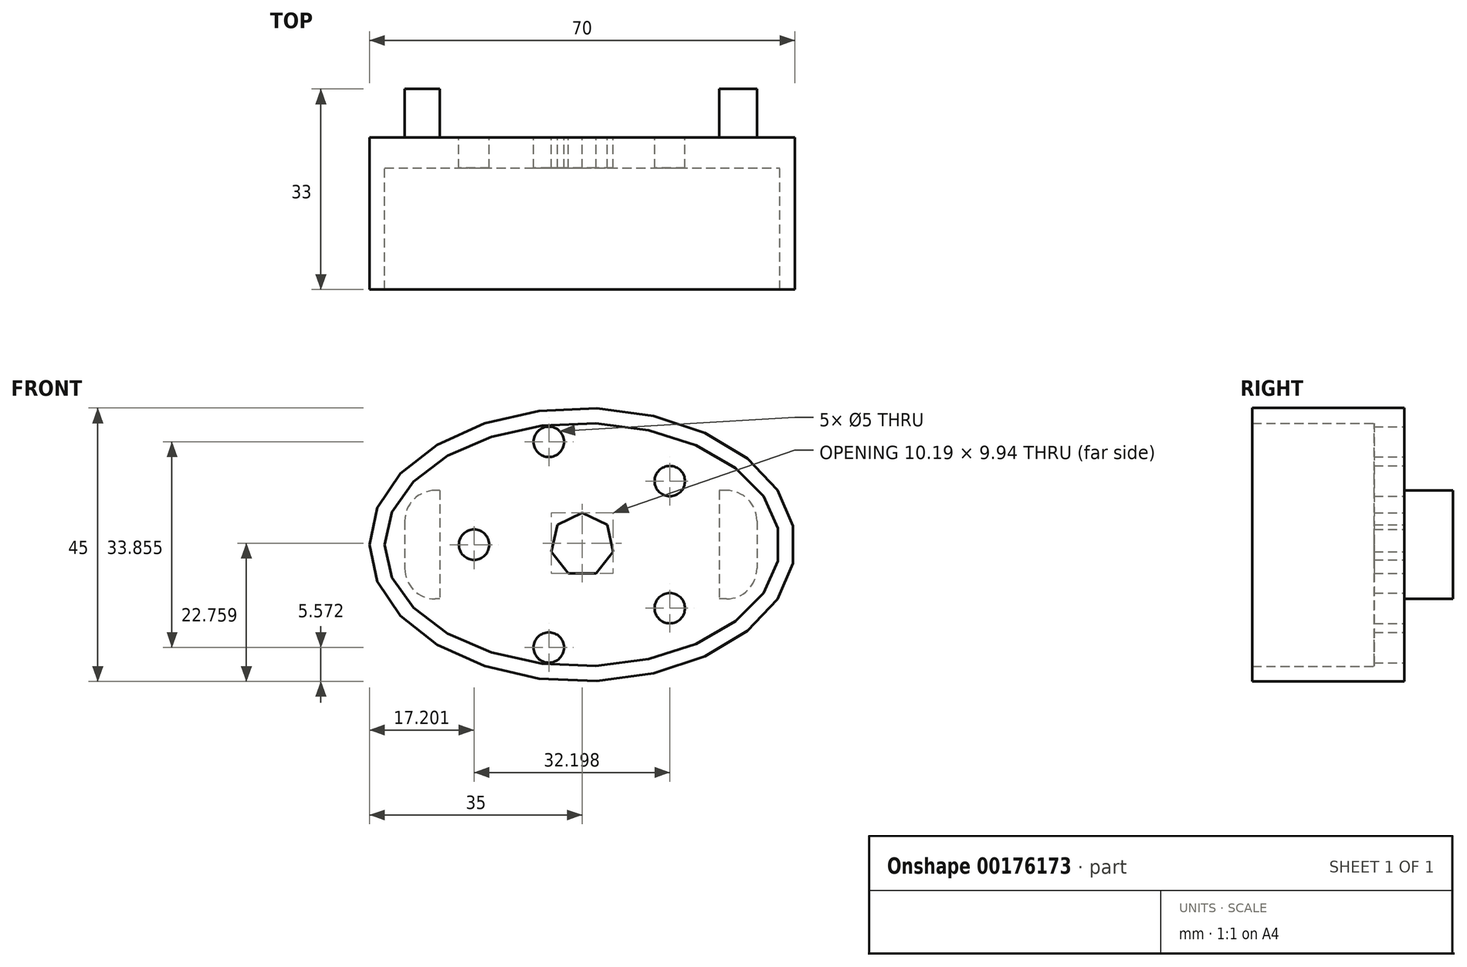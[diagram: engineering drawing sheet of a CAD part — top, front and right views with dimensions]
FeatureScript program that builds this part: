
annotation { "Feature Type Name" : "Feature", "Feature Type Description" : "" }
export const myFeature = defineFeature(function(context is Context, id is Id, definition is map)
    precondition{}
    {
        {
            var Q0;
            Q0=qCreatedBy(makeId("Front.planeOp"),FACE);
            var sketch = newSketch(context, id + "F0", { "sketchPlane" : qUnion([Q0])});
            skEllipse(sketch, "E0", {"center": v(0, 0) * mm, "majorRadius": 35 * mm, "minorRadius": 22.5 * mm, "majorAxis": v(-1, 0)});
            skSolve(sketch);
        }
        {
            var Q0;
            Q0=makeQuery(id+"F0.imprint","IMPRINT",FACE,{"disambiguationData":[TD([[makeQuery(id+"F0.imprint","IMPRINT",EDGE,{"derivedFrom":sQuery(id+"F0.wireOp",EDGE,"E0")}),1.0]])]});
            extrude(context, id + "F1", {"entities" : qUnion([Q0]), "depth" : 5 * mm});
        }
        {
            var Q0;
            Q0=makeQuery(id+"F1.opExtrude","CAP_FACE",FACE,{"disambiguationData":[OSD([sQuery(id+"F0.wireOp",EDGE,"E0")])],"isStart":false});
            var sketch = newSketch(context, id + "F2", { "sketchPlane" : qUnion([Q0])});
            skEllipse(sketch, "E1", {"center": v(0, 0) * mm, "majorRadius": 32.5 * mm, "minorRadius": 20 * mm, "majorAxis": v(-1, 0)});
            skSolve(sketch);
        }
        {
            var Q0;
            Q0=makeQuery(id+"F2.imprint","IMPRINT",FACE,{"disambiguationData":[TD([[makeQuery(id+"F2.imprint","IMPRINT",EDGE,{"derivedFrom":sQuery(id+"F2.wireOp",EDGE,"E1")}),-1.0]])]});
            extrude(context, id + "F3", {"entities" : qUnion([Q0]), "operationType" : NewBodyOperationType.ADD, "depth" : 20 * mm});
        }
        {
            var Q0;
            Q0=qCreatedBy(makeId("Front.planeOp"),FACE);
            var sketch = newSketch(context, id + "F4", { "sketchPlane" : qUnion([Q0])});
            skCircle(sketch, "E2", {"center": v(-17.8, 0) * mm, "radius": 2.5 * mm});
            skCircle(sketch, "E3.1.0", {"center": v(-5.5, -16.93) * mm, "radius": 2.5 * mm});
            skCircle(sketch, "E3.2.0", {"center": v(14.4, -10.46) * mm, "radius": 2.5 * mm});
            skCircle(sketch, "E3.3.0", {"center": v(14.4, 10.46) * mm, "radius": 2.5 * mm});
            skCircle(sketch, "E3.4.0", {"center": v(-5.5, 16.93) * mm, "radius": 2.5 * mm});
            skPoint(sketch, "E3.center", {"position": v(0, 0) * mm});
            skSolve(sketch);
        }
        {
            var Q0;
            Q0=makeQuery(id+"F1.opExtrude","CAP_FACE",FACE,{"disambiguationData":[OSD([sQuery(id+"F0.wireOp",EDGE,"E0")])],"isStart":true});
            var sketch = newSketch(context, id + "F5", { "sketchPlane" : qUnion([Q0])});
            skSolve(sketch);
        }
        {
            var Q0;
            Q0=makeQuery(id+"F4.imprint","IMPRINT",FACE,{"disambiguationData":[TD([[makeQuery(id+"F4.imprint","IMPRINT",EDGE,{"derivedFrom":sQuery(id+"F4.wireOp",EDGE,"E3.1.0")}),1.0]])]});
            var Q1;
            Q1=makeQuery(id+"F4.imprint","IMPRINT",FACE,{"disambiguationData":[TD([[makeQuery(id+"F4.imprint","IMPRINT",EDGE,{"derivedFrom":sQuery(id+"F4.wireOp",EDGE,"E3.2.0")}),1.0]])]});
            var Q2;
            Q2=makeQuery(id+"F4.imprint","IMPRINT",FACE,{"disambiguationData":[TD([[makeQuery(id+"F4.imprint","IMPRINT",EDGE,{"derivedFrom":sQuery(id+"F4.wireOp",EDGE,"E3.3.0")}),1.0]])]});
            var Q3;
            Q3=makeQuery(id+"F4.imprint","IMPRINT",FACE,{"disambiguationData":[TD([[makeQuery(id+"F4.imprint","IMPRINT",EDGE,{"derivedFrom":sQuery(id+"F4.wireOp",EDGE,"E3.4.0")}),1.0]])]});
            var Q4;
            Q4=makeQuery(id+"F4.imprint","IMPRINT",FACE,{"disambiguationData":[TD([[makeQuery(id+"F4.imprint","IMPRINT",EDGE,{"derivedFrom":sQuery(id+"F4.wireOp",EDGE,"E2")}),1.0]])]});
            extrude(context, id + "F6", {"entities" : qUnion([Q0, Q1, Q2, Q3, Q4]), "operationType" : NewBodyOperationType.REMOVE, "endBound" : BoundingType.THROUGH_ALL, "depth" : 25 * mm});
        }
        {
            var Q0;
            Q0=makeQuery(id+"F5.imprint","IMPRINT",FACE,{"disambiguationData":[TD([[makeQuery(id+"F5.imprint","IMPRINT",EDGE,{"derivedFrom":makeQuery(id+"F1.opExtrude","CAP_EDGE",EDGE,{"disambiguationData":[OSD([sQuery(id+"F0.wireOp",EDGE,"E0")])],"isStart":true})}),-1.0]])]});
            var sketch = newSketch(context, id + "F7", { "sketchPlane" : qUnion([Q0])});
            skCircle(sketch, "E4.cCircle", {"center": v(0, 0) * mm, "radius": 4.7 * mm, "construction": true});
            skLineSegment(sketch, "E4.0", {"start": v(2.27, -4.7) * mm, "end": v(-2.27, -4.7) * mm});
            skLineSegment(sketch, "E4.1", {"start": v(-2.27, -4.7) * mm, "end": v(-5.1, -1.16) * mm});
            skLineSegment(sketch, "E4.2", {"start": v(-5.1, -1.16) * mm, "end": v(-4.09, 3.26) * mm});
            skLineSegment(sketch, "E4.3", {"start": v(-4.09, 3.26) * mm, "end": v(0, 5.23) * mm});
            skLineSegment(sketch, "E4.4", {"start": v(0, 5.23) * mm, "end": v(4.09, 3.26) * mm});
            skLineSegment(sketch, "E4.5", {"start": v(4.09, 3.26) * mm, "end": v(5.1, -1.16) * mm});
            skLineSegment(sketch, "E4.6", {"start": v(5.1, -1.16) * mm, "end": v(2.27, -4.7) * mm});
            skPoint(sketch, "E4.0.midPoint", {"position": v(0, -4.7) * mm});
            skSolve(sketch);
        }
        {
            var Q0;
            Q0 = qSketchRegion(id + "F7", true);
            extrude(context, id + "F8", {"entities" : qUnion([Q0]), "operationType" : NewBodyOperationType.REMOVE, "endBound" : BoundingType.THROUGH_ALL, "oppositeDirection" : true, "depth" : 25 * mm});
        }
        {
            var Q0;
            Q0=makeQuery(id+"F5.imprint","IMPRINT",FACE,{"disambiguationData":[TD([[makeQuery(id+"F5.imprint","IMPRINT",EDGE,{"derivedFrom":makeQuery(id+"F1.opExtrude","CAP_EDGE",EDGE,{"disambiguationData":[OSD([sQuery(id+"F0.wireOp",EDGE,"E0")])],"isStart":true})}),-1.0]])]});
            var sketch = newSketch(context, id + "F9", { "sketchPlane" : qUnion([Q0])});
            skLineSegment(sketch, "E5.bottom", {"start": v(-23.73, 8.92) * mm, "end": v(-22.54, 8.92) * mm});
            skLineSegment(sketch, "E5.top", {"start": v(-23.73, -8.92) * mm, "end": v(-22.54, -8.92) * mm});
            skLineSegment(sketch, "E5.left", {"start": v(-28.73, 3.92) * mm, "end": v(-28.73, -3.92) * mm});
            skLineSegment(sketch, "E5.right", {"start": v(-22.54, 8.92) * mm, "end": v(-22.54, -8.92) * mm});
            skPoint(sketch, "E5.middle", {"position": v(-25.63, 0) * mm});
            skLineSegment(sketch, "E6.bottom", {"start": v(23.43, 8.92) * mm, "end": v(24.2, 8.92) * mm});
            skLineSegment(sketch, "E6.top", {"start": v(23.43, -8.92) * mm, "end": v(24.2, -8.92) * mm});
            skLineSegment(sketch, "E6.left", {"start": v(23.43, 8.92) * mm, "end": v(23.43, -8.92) * mm});
            skLineSegment(sketch, "E6.right", {"start": v(29.2, 3.92) * mm, "end": v(29.2, -3.92) * mm});
            skPoint(sketch, "E6.middle", {"position": v(26.31, 0) * mm});
            skPoint(sketch, "E6.cornerSnap0", {"position": v(-25.63, 8.92) * mm});
            skPoint(sketch, "E7.visualSharp", {"position": v(-28.73, 8.92) * mm});
            skArc(sketch, "E7.filletArc", {"start": v(-23.73, 8.92) * mm, "mid": v(-27.26, 7.46) * mm, "end": v(-28.73, 3.92) * mm});
            skPoint(sketch, "E8.visualSharp", {"position": v(-28.73, -8.92) * mm});
            skArc(sketch, "E8.filletArc", {"start": v(-28.73, -3.92) * mm, "mid": v(-27.26, -7.46) * mm, "end": v(-23.73, -8.92) * mm});
            skPoint(sketch, "E9.visualSharp", {"position": v(29.2, 8.92) * mm});
            skArc(sketch, "E9.filletArc", {"start": v(29.2, 3.92) * mm, "mid": v(27.74, 7.46) * mm, "end": v(24.2, 8.92) * mm});
            skPoint(sketch, "E10.visualSharp", {"position": v(29.2, -8.92) * mm});
            skArc(sketch, "E10.filletArc", {"start": v(24.2, -8.92) * mm, "mid": v(27.74, -7.46) * mm, "end": v(29.2, -3.92) * mm});
            skSolve(sketch);
        }
        {
            var Q0;
            Q0 = qSketchRegion(id + "F9", true);
            extrude(context, id + "F10", {"entities" : qUnion([Q0]), "operationType" : NewBodyOperationType.ADD, "depth" : 8 * mm});
        }
    });
